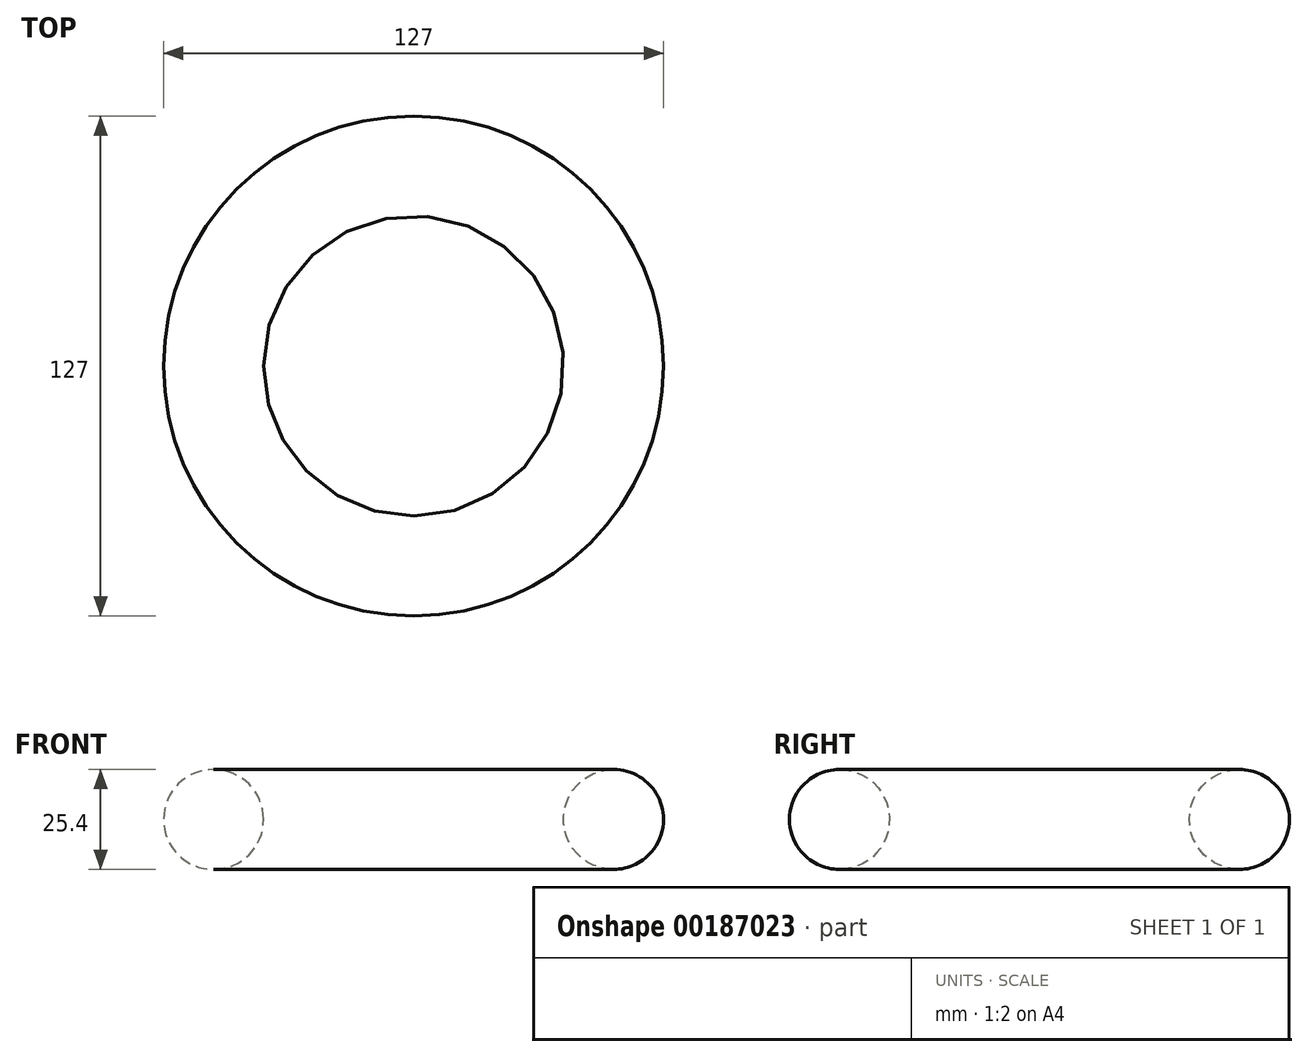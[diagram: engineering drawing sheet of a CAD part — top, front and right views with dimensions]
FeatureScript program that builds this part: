
annotation { "Feature Type Name" : "Feature", "Feature Type Description" : "" }
export const myFeature = defineFeature(function(context is Context, id is Id, definition is map)
    precondition{}
    {
        {
            var Q0;
            Q0=qCreatedBy(makeId("Front.planeOp"),FACE);
            var sketch = newSketch(context, id + "F0", { "sketchPlane" : qUnion([Q0])});
            skCircle(sketch, "E0", {"center": v(50.8, 0) * mm, "radius": 12.7 * mm});
            skLineSegment(sketch, "E1", {"start": v(0, 0) * mm, "end": v(0, 33.15) * mm});
            skSolve(sketch);
        }
        {
            var Q0;
            Q0=makeQuery(id+"F0.imprint","IMPRINT",FACE,{"disambiguationData":[TD([[makeQuery(id+"F0.imprint","IMPRINT",EDGE,{"derivedFrom":sQuery(id+"F0.wireOp",EDGE,"E0")}),1.0]])]});
            var Q1;
            Q1=sQuery(id+"F0.wireOp",EDGE,"E1");
            revolve(context, id + "F1", {"entities" : qUnion([Q0]), "axis" : qUnion([Q1]), "revolveType" : RevolveType.FULL});
        }
    });
